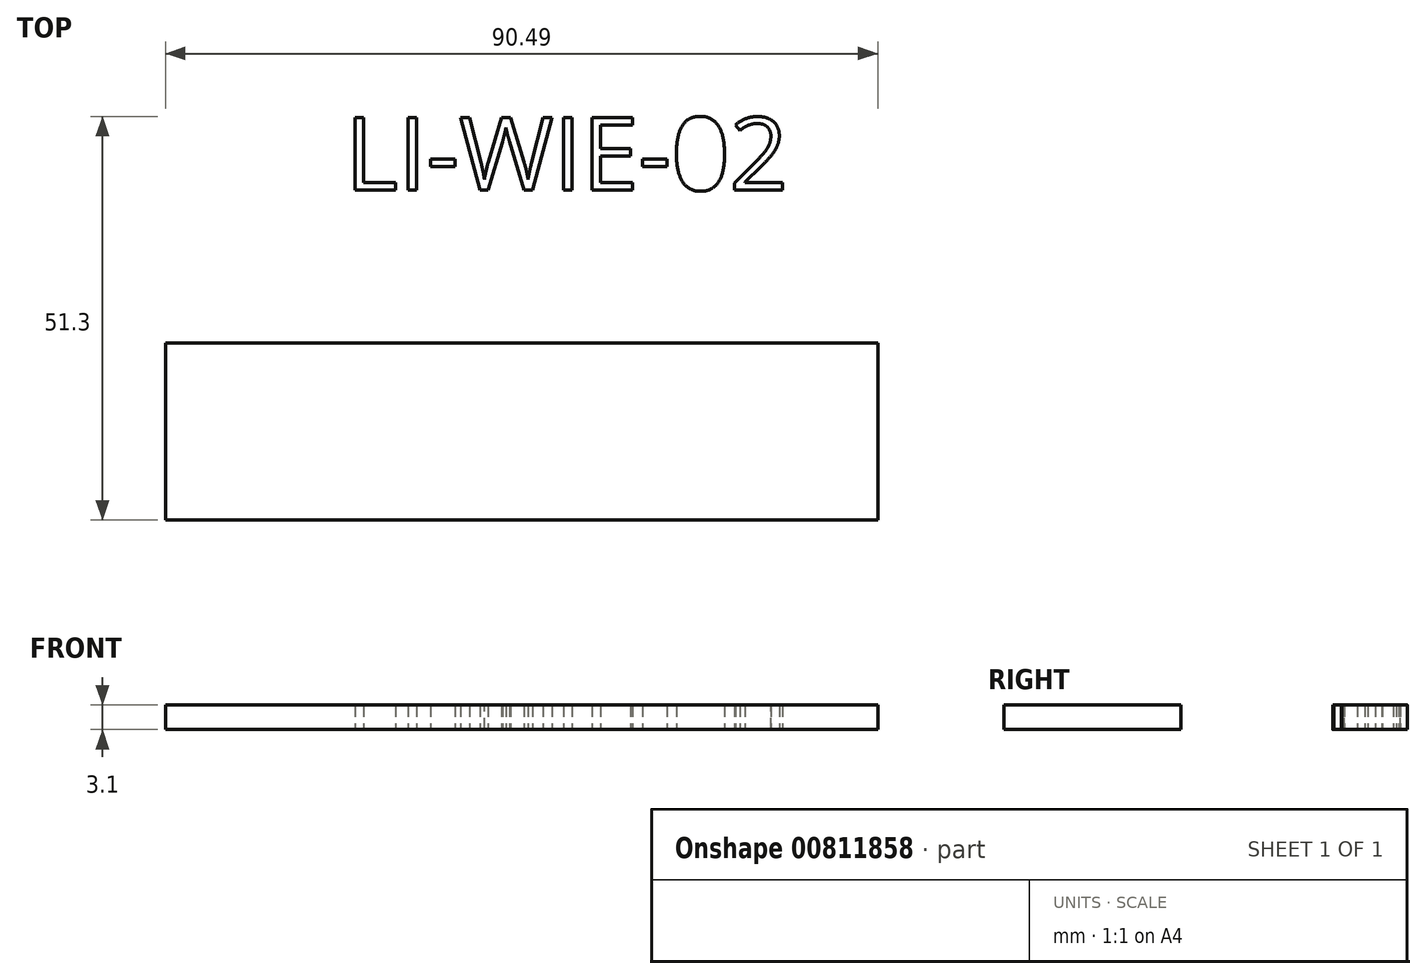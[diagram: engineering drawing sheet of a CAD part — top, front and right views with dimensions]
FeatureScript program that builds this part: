
annotation { "Feature Type Name" : "Feature", "Feature Type Description" : "" }
export const myFeature = defineFeature(function(context is Context, id is Id, definition is map)
    precondition{}
    {
        {
            var Q0;
            Q0=qCreatedBy(makeId("Top.planeOp"),FACE);
            var sketch = newSketch(context, id + "F0", { "sketchPlane" : qUnion([Q0])});
            skLineSegment(sketch, "E0.bottom", {"start": v(0, 35.58) * mm, "end": v(-90.49, 35.58) * mm});
            skLineSegment(sketch, "E0.top", {"start": v(0, 13.07) * mm, "end": v(-90.49, 13.07) * mm});
            skLineSegment(sketch, "E0.left", {"start": v(0, 35.58) * mm, "end": v(0, 13.07) * mm});
            skLineSegment(sketch, "E0.right", {"start": v(-90.49, 35.58) * mm, "end": v(-90.49, 13.07) * mm});
            skText(sketch, "E1", { "text": "LI-WIE-02", "fontName": "OpenSans-Regular.ttf"});
            const initialGuessF0  = {"E1": [-0.06767, 0.05498, 1, 0, 0.00932]};
            skSetInitialGuess(sketch, initialGuessF0);
            skSolve(sketch);
        }
        {
            var Q0;
            Q0 = qSketchRegion(id + "F0", true);
            var Q1;
            Q1=makeQuery(id+"F0.imprint","IMPRINT",FACE,{"disambiguationData":[TD([[makeQuery(id+"F0.imprint","IMPRINT",EDGE,{"derivedFrom":sQuery(id+"F0.wireOp",EDGE,"E1.sketch_text.stroke-62")}),1.0]])]});
            extrude(context, id + "F1", {"entities" : qUnion([Q0, Q1]), "depth" : 3.1 * mm, "offsetDistance" : 25 * mm});
        }
    });
